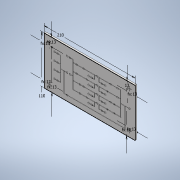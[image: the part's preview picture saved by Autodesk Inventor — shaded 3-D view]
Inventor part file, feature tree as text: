
AUTODESK INVENTOR PART (.ipt)
format: ipt  version: 2021 (Build 250183000, 183)  size: 719,360 bytes
history: native  units: in
note: dims shown in document units (in); Inventor stores cm internally (conversion verified against a paired STEP export)
features: other x9, extrude x4, hole x2, surface_op x1
ambient origin geometry x8: Origin, YZ Plane, XZ Plane, XY Plane, X Axis, Y Axis, Z Axis, Center Point
bodies: Solid1 (feature_tree)
feature tree (16):
  other  "points for corner holes"
  extrude  "Extrusion base plate"  Depth=6.6929in
  other  "plane above base plate to create rib"
  other  "channels and points for valves and for connectors"
  other  "channels as rib"
  extrude  "extrusion of rib to get cutout"  Depth=8.6614in
  other  "valve shape"
  extrude  "valve space extrusion"  Depth=0.1969in
  extrude  "valve bar extrusion"  Depth=0.3543in
  other  "all valve spaces"
  other  "projected point for every hole"
  hole  "holes for connectors"  [1 undecoded]
  hole  "holes in corners"  [1 undecoded]
  other  "valve bar shape"
  other  "Projected points for every valve"
  surface_op  "surface of rib as sketch"
note: 2 required parameter values undecoded (feature->parameter linkage not recoverable at this tier; creation-order binding heuristic only, values carry confidence <= 0.55)
